# Revit family: IS_Mara_A9011_BIM_FR
name_source: partatom
category: Plumbing Fixtures
revit_build: Autodesk Revit 2017 (Build: 20160225_1515(x64)
units: mm (PartAtom-declared; Revit-internal decimal feet)

## family parameters
Always vertical = No
Cut with Voids When Loaded = No
OmniClass Number = 23.45.55.17
OmniClass Title = Mixing Faucets
Part Type = Normal
Room Calculation Point = No
Round Connector Dimension = Use Diameter
Shared = No
Work Plane-Based = No

## types (1)
- A9011AA - MARA MITIGEUR BIDET AV VIDAGE CHROME
    Accessoires = www.idealstandard.be
    Auteur = Ideal Standard
    BOSUseNativeGeometries = 1
    Bim-NomDuProjet = ISI_IdealStandard_BidetWaterSupplyFittings_MARA_A9011AA
    Caractéristiques = MARA BID MXR R-MTD PU/METAL EPDM 3/8
    CodeBarre = 3800861012221
    ConseilsDInstallation = www.idealstandard.be
    Cost = 0 $
    Couleur = Chrome
    CoûtDeRemplacement = 0
    DateDeCréation = 2018_08_15
    Description = MARA Mitigeur bidet monotrou
    Dimensions = 149 x 50 x 124mm
    Espace = Interne
    Finition = Chrome
    Forme = Complexe
    Hauteur = 149 mm
    IfcExportAs = FAUCETS
    IfcExportType = IfcValveType
    InformationsProduit = www.idealstandard.be
    Largeur = 50 mm
    LienUtile = www.idealstandard.be
    Longueur = 124 mm
    Manufacturer = www.idealstandard.be
    Marque = Ideal Standard
    Matériel = Brass
    Model = A9011AA
    Profondeur = 0 mm  [stored 0 ft]
    Raccordement = Plomberie
    Révision = 1
    TestDePression = 0
    TypeDeRobinetterie = Bidet Mixer
    URL = www.idealstandard.be
    Uniclass2015Code = Pr_40_20_06_11
    Uniclass2015Title = Bidets
    Uniclass2015Version = Products v1.1
    UnitéDeMesure = Millimètres
    UnitéDeTemps = An
    UnitéMonétaire = €
    UrlDuFabricant = www.idealstandard.be
    Version = 1

note: [stored X ft] marks values corroborated as IEEE doubles in the binary element streams (Revit-internal decimal feet)

## geometry (parser evidence)
native form markers: Sweep x2
no freeform markers — native parametric forms only
